# Revit family: Rohrschelle Sprinkler HDC, M 8, Ø 20- 65
name_source: partatom
category: HLS-Bauteile
revit_build: Autodesk Revit 2017 (Build: 20190507_1515(x64)
units: mm (PartAtom-declared; Revit-internal decimal feet)

## family parameters
Arbeitsebenenbasiert = Ja
Beim Laden mit Abzugskörper schneiden = Nein
Bemaßung runder Anschluss = Durchmesser verwenden
Gemeinsam genutzt = Ja
Immer vertikal = Nein
Raumberechnungspunkt = Nein
Teiletyp = Normal

## types (6) — shared parameters
A = 20 mm  [stored 0.0656168 ft]
Anschluss = M8
Bauart = zweiteilig
DVS = 5 mm  [stored 0.0164042 ft]
Fabrikat = Jiangmen Eurofix
Firma = MEFA Befestigungs- und Montagesysteme GmbH
Gewicht pro Bauteil = 0.00 kg
H1 = 2 mm  [stored 0.00656168 ft]
H2 = 5 mm  [stored 0.0164042 ft]
HGA = 17 mm
Kurztext1 = Rohrschelle HDC 30x2,5
MB = 30 mm  [stored 0.0984252 ft]
MD = 3 mm  [stored 0.00984252 ft]
Material = Stahl
Materialmaße = 30x2,5 mm
Mengeneinheit = St
Oberflaeche = galvanisch verzinkt
Verschluss-Schraube = M8
Vorgabe-Ansicht = 1219 mm
max. zul. Last horizontal = 0.00 kN
max. zul. Last vertikal = 0.00 kN
zero-valued in all types: DS, Nennweite DN Rohr, Rohraußendurchmesser, Stärke Material

## per-type parameters (varying)
- RS Sprinkler HDC, M 8, Ø 20- 24: AB=1 mm  [stored 0.00328084 ft]; Achsabstand=44 mm; Anschlußhöhe=15 mm; Artikelnummer=47300020; B=71 mm  [stored 0.23294 ft]; Breite=66 mm  [stored 0.216535 ft]; D=21 mm  [stored 0.0688976 ft]; D0=21 mm  [stored 0.0688976 ft]; DF1=22 mm  [stored 0.0721785 ft]; DF2=20 mm  [stored 0.0656168 ft]; Dmax=24 mm  [stored 0.0787402 ft]; Dmin=20 mm  [stored 0.0656168 ft]; EAN=4250928458148; Gewicht=0.14 kg; H=43 mm  [stored 0.141076 ft]; Höhe=42 mm; Kurztext2=20 - 24 mm M8; R=11 mm; RM=14 mm  [stored 0.0459318 ft]; Rohraußendurchmesser Zoll=1/2 Zoll; S=49 mm  [stored 0.160761 ft]; max. Rohraußendurchmesser=24 mm  [stored 0.0787402 ft]; max. zul. Last=2.50 kN; min. Rohraußendurchmesser=20 mm  [stored 0.0656168 ft]; vpe=50 St
- RS Sprinkler HDC, M 8, Ø 25- 30: AB=1 mm  [stored 0.00328084 ft]; Achsabstand=50 mm; Anschlußhöhe=17 mm; Artikelnummer=47300025; B=76 mm  [stored 0.249344 ft]; Breite=71 mm  [stored 0.23294 ft]; D=26 mm; D0=26 mm; DF1=21 mm  [stored 0.0688976 ft]; DF2=20 mm  [stored 0.0656168 ft]; Dmax=30 mm  [stored 0.0984252 ft]; Dmin=25 mm  [stored 0.082021 ft]; EAN=4250928458155; Gewicht=0.15 kg; H=48 mm  [stored 0.15748 ft]; Höhe=50 mm; Kurztext2=25 - 30 mm M8; R=13 mm; RM=16 mm  [stored 0.0524934 ft]; Rohraußendurchmesser Zoll=3/4 Zoll; S=55 mm  [stored 0.180446 ft]; max. Rohraußendurchmesser=30 mm  [stored 0.0984252 ft]; max. zul. Last=2.50 kN; min. Rohraußendurchmesser=25 mm  [stored 0.082021 ft]; vpe=50 St
- RS Sprinkler HDC, M 8, Ø 31- 35: AB=1 mm  [stored 0.00328084 ft]; Achsabstand=55 mm; Anschlußhöhe=16 mm; Artikelnummer=47300031; B=82 mm; Breite=77 mm; D=32 mm  [stored 0.104987 ft]; D0=32 mm  [stored 0.104987 ft]; DF1=22 mm  [stored 0.0721785 ft]; DF2=20 mm  [stored 0.0656168 ft]; Dmax=35 mm  [stored 0.114829 ft]; Dmin=31 mm  [stored 0.101706 ft]; EAN=4250928458162; Gewicht=0.16 kg; H=54 mm; Höhe=55 mm; Kurztext2=31 - 35 mm M8; R=16 mm  [stored 0.0524934 ft]; RM=19 mm; Rohraußendurchmesser Zoll=1 Zoll; S=60 mm  [stored 0.19685 ft]; max. Rohraußendurchmesser=35 mm  [stored 0.114829 ft]; max. zul. Last=2.50 kN; min. Rohraußendurchmesser=31 mm  [stored 0.101706 ft]; vpe=50 St
- RS Sprinkler HDC, M 8, Ø 40- 45: AB=2 mm  [stored 0.00656168 ft]; Achsabstand=66 mm; Anschlußhöhe=16 mm; Artikelnummer=47300040; B=93 mm; Breite=88 mm; D=42 mm  [stored 0.137795 ft]; D0=42 mm  [stored 0.137795 ft]; DF1=22 mm  [stored 0.0721785 ft]; DF2=21 mm  [stored 0.0688976 ft]; Dmax=45 mm  [stored 0.147638 ft]; Dmin=40 mm  [stored 0.131234 ft]; EAN=4250928458179; Gewicht=0.17 kg; H=64 mm  [stored 0.209974 ft]; Höhe=65 mm; Kurztext2=40 - 45 mm M8; R=21 mm  [stored 0.0688976 ft]; RM=25 mm  [stored 0.082021 ft]; Rohraußendurchmesser Zoll=1 1/4 Zoll; S=71 mm  [stored 0.23294 ft]; max. Rohraußendurchmesser=45 mm  [stored 0.147638 ft]; max. zul. Last=1.50 kN; min. Rohraußendurchmesser=40 mm  [stored 0.131234 ft]; vpe=50 St
- RS Sprinkler HDC, M 8, Ø 48- 53: AB=2 mm  [stored 0.00656168 ft]; Achsabstand=74 mm; Anschlußhöhe=16 mm; Artikelnummer=47300048; B=101 mm; Breite=96 mm; D=50 mm  [stored 0.164042 ft]; D0=50 mm  [stored 0.164042 ft]; DF1=22 mm  [stored 0.0721785 ft]; DF2=21 mm  [stored 0.0688976 ft]; Dmax=53 mm  [stored 0.173885 ft]; Dmin=48 mm  [stored 0.15748 ft]; EAN=4250928458186; Gewicht=0.19 kg; H=72 mm  [stored 0.23622 ft]; Höhe=73 mm; Kurztext2=48 - 53 mm M8; R=25 mm  [stored 0.082021 ft]; RM=29 mm; Rohraußendurchmesser Zoll=1 1/2 Zoll; S=79 mm; max. Rohraußendurchmesser=53 mm  [stored 0.173885 ft]; max. zul. Last=2.50 kN; min. Rohraußendurchmesser=48 mm  [stored 0.15748 ft]; vpe=50 St
- RS Sprinkler HDC, M 8, Ø 60- 65: AB=2 mm  [stored 0.00656168 ft]; Achsabstand=87 mm; Anschlußhöhe=16 mm; Artikelnummer=47300061; B=113 mm; Breite=108 mm; D=62 mm  [stored 0.203412 ft]; D0=62 mm  [stored 0.203412 ft]; DF1=21 mm  [stored 0.0688976 ft]; DF2=22 mm  [stored 0.0721785 ft]; Dmax=65 mm  [stored 0.213255 ft]; Dmin=60 mm  [stored 0.19685 ft]; EAN=4250928458193; Gewicht=0.22 kg; H=84 mm; Höhe=85 mm; Kurztext2=60 - 65 mm M8; R=31 mm  [stored 0.101706 ft]; RM=35 mm  [stored 0.114829 ft]; Rohraußendurchmesser Zoll=2 Zoll; S=92 mm; max. Rohraußendurchmesser=65 mm  [stored 0.213255 ft]; max. zul. Last=2.50 kN; min. Rohraußendurchmesser=60 mm  [stored 0.19685 ft]; vpe=25 St

note: [stored X ft] marks values corroborated as IEEE doubles in the binary element streams (Revit-internal decimal feet)

## geometry (parser evidence)
native form markers: Sweep x3
no freeform markers — native parametric forms only
